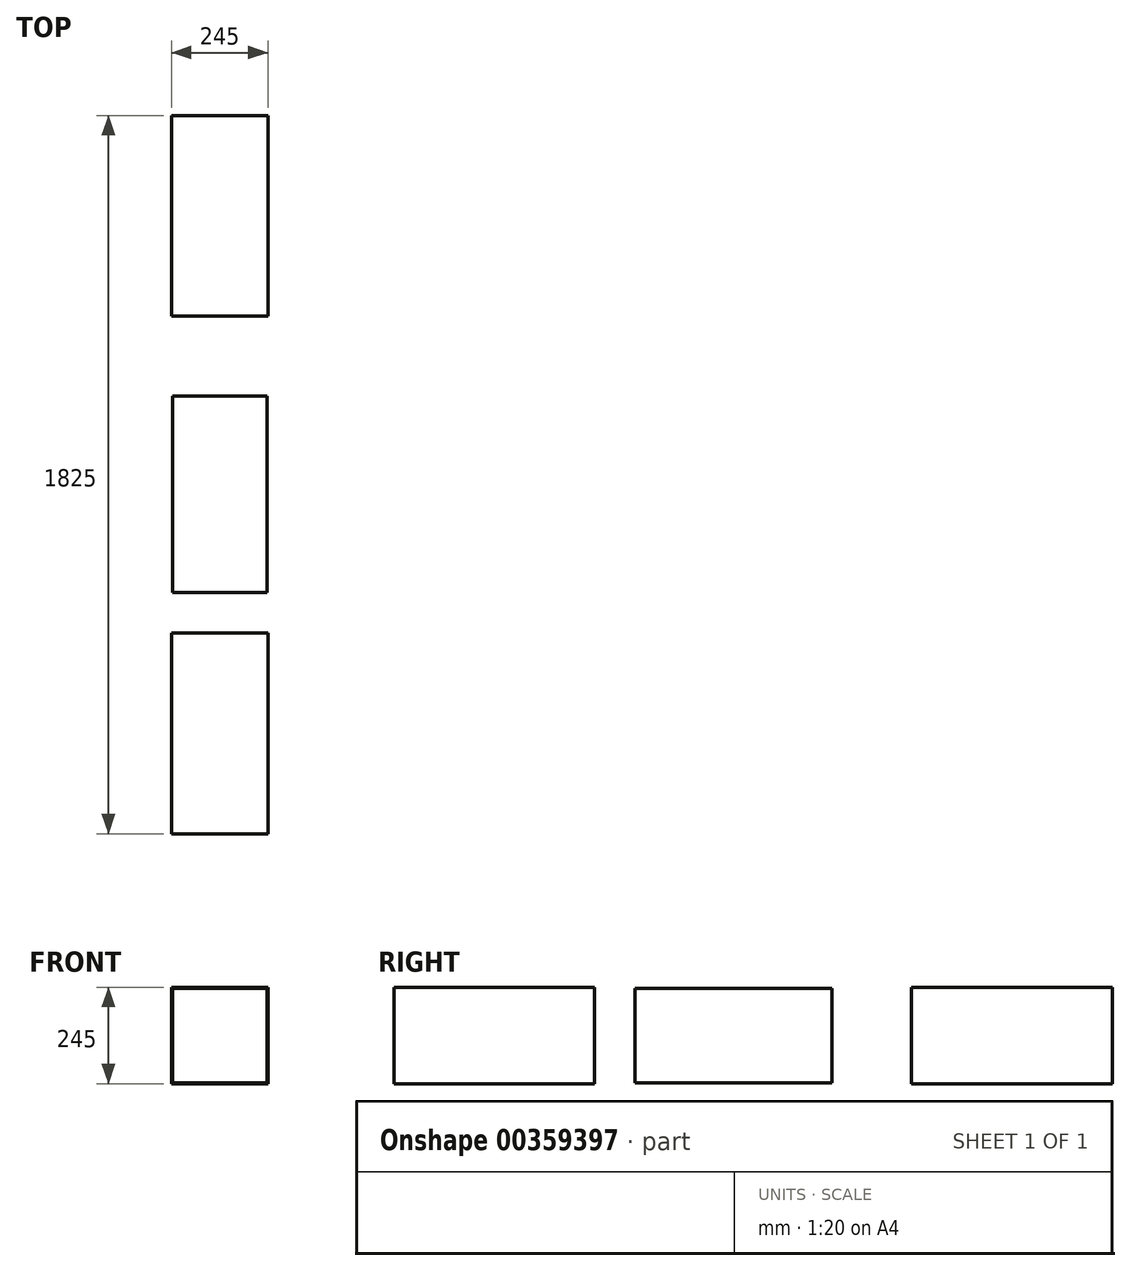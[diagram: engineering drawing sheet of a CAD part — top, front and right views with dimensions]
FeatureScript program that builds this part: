
annotation { "Feature Type Name" : "Feature", "Feature Type Description" : "" }
export const myFeature = defineFeature(function(context is Context, id is Id, definition is map)
    precondition{}
    {
        {
            var Q0;
            Q0=qCreatedBy(makeId("Front.planeOp"),FACE);
            cPlane(context, id + "F0", {"entities" : qUnion([Q0]), "cplaneType" : CPlaneType.OFFSET, "offset" : 2525 * mm, "width" : 150 * mm, "height" : 150 * mm});
        }
        {
            var Q0;
            Q0=qCreatedBy(makeId("Front.planeOp"),FACE);
            cPlane(context, id + "F1", {"entities" : qUnion([Q0]), "cplaneType" : CPlaneType.OFFSET, "offset" : 300 * mm, "width" : 150 * mm, "height" : 150 * mm});
        }
        {
            var Q0;
            Q0=qCreatedBy(id+"F0.planeOp",FACE);
            cPlane(context, id + "F2", {"entities" : qUnion([Q0]), "cplaneType" : CPlaneType.OFFSET, "offset" : 400 * mm, "oppositeDirection" : true, "width" : 150 * mm, "height" : 150 * mm});
        }
        {
            var Q0;
            Q0=qCreatedBy(makeId("Top.planeOp"),FACE);
            cPlane(context, id + "F3", {"entities" : qUnion([Q0]), "cplaneType" : CPlaneType.OFFSET, "offset" : 80 * mm, "width" : 150 * mm, "height" : 150 * mm});
        }
        {
            var Q0;
            Q0=qCreatedBy(makeId("Right.planeOp"),FACE);
            var sketch = newSketch(context, id + "F4", { "sketchPlane" : qUnion([Q0])});
            skSolve(sketch);
        }
        {
            var Q0;
            Q0=qCreatedBy(id+"F1.planeOp",FACE);
            var sketch = newSketch(context, id + "F5", { "sketchPlane" : qUnion([Q0])});
            skLineSegment(sketch, "E0.bottom", {"start": v(-122.5, 202.5) * mm, "end": v(122.5, 202.5) * mm});
            skLineSegment(sketch, "E0.top", {"start": v(-122.5, -42.5) * mm, "end": v(122.5, -42.5) * mm});
            skLineSegment(sketch, "E0.left", {"start": v(-122.5, 202.5) * mm, "end": v(-122.5, -42.5) * mm});
            skLineSegment(sketch, "E0.right", {"start": v(122.5, 202.5) * mm, "end": v(122.5, -42.5) * mm});
            skPoint(sketch, "E0.middle", {"position": v(0, 80) * mm});
            skSolve(sketch);
        }
        {
            var Q0;
            Q0=qCreatedBy(id+"F2.planeOp",FACE);
            var sketch = newSketch(context, id + "F6", { "sketchPlane" : qUnion([Q0])});
            skLineSegment(sketch, "E1.bottom", {"start": v(-122.5, 202.5) * mm, "end": v(122.5, 202.5) * mm});
            skLineSegment(sketch, "E1.top", {"start": v(-122.5, -42.5) * mm, "end": v(122.5, -42.5) * mm});
            skLineSegment(sketch, "E1.left", {"start": v(-122.5, 202.5) * mm, "end": v(-122.5, -42.5) * mm});
            skLineSegment(sketch, "E1.right", {"start": v(122.5, 202.5) * mm, "end": v(122.5, -42.5) * mm});
            skPoint(sketch, "E1.middle", {"position": v(0, 80) * mm});
            skSolve(sketch);
        }
        {
            var Q0;
            Q0 = qConstructionFilter(qBodyType(qCreatedBy(id + "F5" ,EDGE), BodyType.WIRE), ConstructionObject.NO);
            extrude(context, id + "F7", {"bodyType" : ToolBodyType.SURFACE, "surfaceEntities" : qUnion([Q0]), "depth" : 510 * mm});
        }
        {
            var Q0;
            Q0 = qSketchRegion(id + "F5", true);
            var Q1;
            Q1 = qConstructionFilter(qBodyType(qCreatedBy(id + "F6" ,EDGE), BodyType.WIRE), ConstructionObject.NO);
            extrude(context, id + "F8", {"entities" : qUnion([Q0]), "bodyType" : ToolBodyType.SURFACE, "surfaceEntities" : qUnion([Q1]), "oppositeDirection" : true, "depth" : 510 * mm});
        }
        {
            var Q0;
            Q0=qCreatedBy(makeId("Front.planeOp"),FACE);
            cPlane(context, id + "F9", {"entities" : qUnion([Q0]), "cplaneType" : CPlaneType.OFFSET, "offset" : (2525 / 2) * mm, "width" : 150 * mm, "height" : 150 * mm});
        }
        {
            var Q0;
            Q0=qCreatedBy(id+"F9.planeOp",FACE);
            var sketch = newSketch(context, id + "F10", { "sketchPlane" : qUnion([Q0])});
            skLineSegment(sketch, "E2.bottom", {"start": v(-120, -40) * mm, "end": v(120, -40) * mm});
            skLineSegment(sketch, "E2.top", {"start": v(-120, 200) * mm, "end": v(120, 200) * mm});
            skLineSegment(sketch, "E2.left", {"start": v(-120, -40) * mm, "end": v(-120, 200) * mm});
            skLineSegment(sketch, "E2.right", {"start": v(120, -40) * mm, "end": v(120, 200) * mm});
            skPoint(sketch, "E2.middle", {"position": v(0, 80) * mm});
            skSolve(sketch);
        }
        {
            var Q0;
            Q0 = qSketchRegion(id + "F10", true);
            var Q1;
            Q1 = qConstructionFilter(qBodyType(qCreatedBy(id + "F10" ,EDGE), BodyType.WIRE), ConstructionObject.NO);
            extrude(context, id + "F11", {"entities" : qUnion([Q0]), "bodyType" : ToolBodyType.SURFACE, "surfaceEntities" : qUnion([Q1]), "endBound" : BoundingType.SYMMETRIC, "depth" : 500 * mm});
        }
    });
